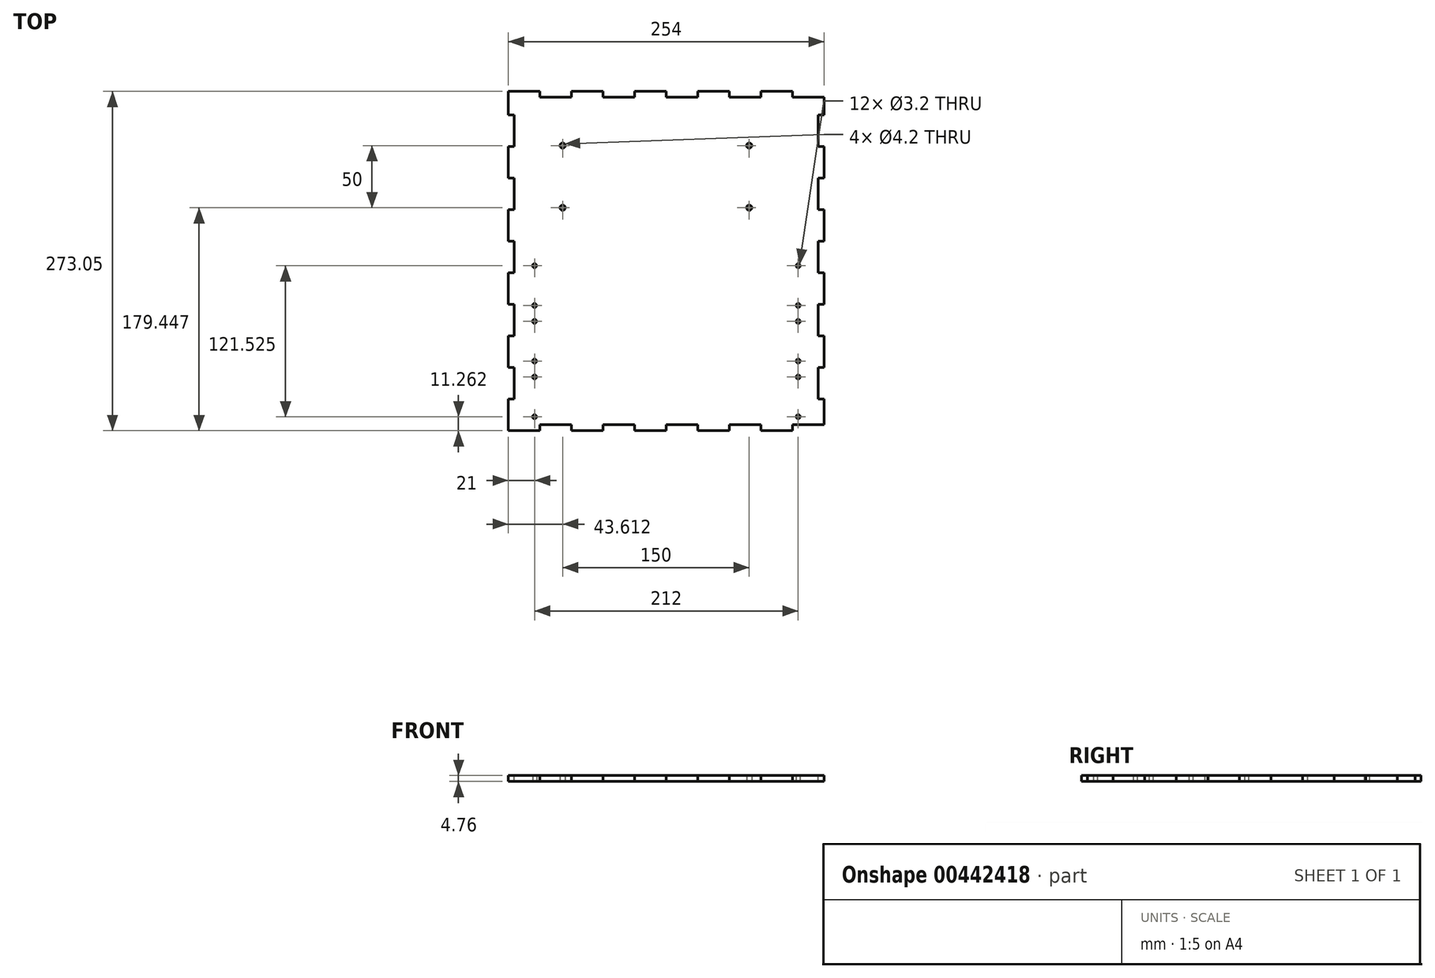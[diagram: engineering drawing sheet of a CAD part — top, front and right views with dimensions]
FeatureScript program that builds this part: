
annotation { "Feature Type Name" : "Feature", "Feature Type Description" : "" }
export const myFeature = defineFeature(function(context is Context, id is Id, definition is map)
    precondition{}
    {
        {
            var Q0;
            Q0=qCreatedBy(makeId("Top.planeOp"),FACE);
            var sketch = newSketch(context, id + "F0", { "sketchPlane" : qUnion([Q0])});
            skLineSegment(sketch, "E0.bottom", {"start": v(0, 0) * mm, "end": v(254, 0) * mm});
            skLineSegment(sketch, "E0.top", {"start": v(0, 273.05) * mm, "end": v(254, 273.05) * mm});
            skLineSegment(sketch, "E0.left", {"start": v(0, 0) * mm, "end": v(0, 273.05) * mm});
            skLineSegment(sketch, "E0.right", {"start": v(254, 0) * mm, "end": v(254, 273.05) * mm});
            skLineSegment(sketch, "E1.0", {"start": v(4.76, 4.76) * mm, "end": v(4.76, 268.29) * mm, "construction": true});
            skLineSegment(sketch, "E1.1", {"start": v(4.76, 4.76) * mm, "end": v(249.24, 4.76) * mm, "construction": true});
            skLineSegment(sketch, "E1.2", {"start": v(249.24, 4.76) * mm, "end": v(249.24, 268.29) * mm, "construction": true});
            skLineSegment(sketch, "E1.3", {"start": v(4.76, 268.29) * mm, "end": v(249.24, 268.29) * mm, "construction": true});
            skCircle(sketch, "E2", {"center": v(21, 11.26) * mm, "radius": 1.6 * mm});
            skCircle(sketch, "E3.0.1.0", {"center": v(21, 43.26) * mm, "radius": 1.6 * mm});
            skLineSegment(sketch, "E3.direction1", {"start": v(21, 11.26) * mm, "end": v(46.4, 11.26) * mm, "construction": true});
            skLineSegment(sketch, "E3.direction2", {"start": v(21, 11.26) * mm, "end": v(21, 43.26) * mm, "construction": true});
            skCircle(sketch, "E4.MirrorC", {"center": v(233, 43.26) * mm, "radius": 1.6 * mm});
            skCircle(sketch, "E5.MirrorC", {"center": v(233, 11.26) * mm, "radius": 1.6 * mm});
            skLineSegment(sketch, "E6.direction1", {"start": v(21, 43.26) * mm, "end": v(46.4, 43.26) * mm, "construction": true});
            skLineSegment(sketch, "E7.bottom", {"start": v(17, 47.26) * mm, "end": v(237, 47.26) * mm, "construction": true});
            skLineSegment(sketch, "E7.top", {"start": v(17, 7.26) * mm, "end": v(237, 7.26) * mm, "construction": true});
            skLineSegment(sketch, "E7.left", {"start": v(17, 47.26) * mm, "end": v(17, 7.26) * mm, "construction": true});
            skLineSegment(sketch, "E7.right", {"start": v(237, 47.26) * mm, "end": v(237, 7.26) * mm, "construction": true});
            skLineSegment(sketch, "E8.0.1.0", {"start": v(17, 92.02) * mm, "end": v(237, 92.02) * mm, "construction": true});
            skLineSegment(sketch, "E8.0.1.1", {"start": v(17, 52.02) * mm, "end": v(237, 52.02) * mm, "construction": true});
            skLineSegment(sketch, "E8.0.1.2", {"start": v(17, 92.02) * mm, "end": v(17, 52.02) * mm, "construction": true});
            skCircle(sketch, "E8.0.1.3", {"center": v(21, 88.02) * mm, "radius": 1.6 * mm});
            skCircle(sketch, "E8.0.1.4", {"center": v(21, 56.02) * mm, "radius": 1.6 * mm});
            skCircle(sketch, "E8.0.1.5", {"center": v(233, 88.02) * mm, "radius": 1.6 * mm});
            skCircle(sketch, "E8.0.1.6", {"center": v(233, 56.02) * mm, "radius": 1.6 * mm});
            skLineSegment(sketch, "E8.0.1.7", {"start": v(237, 92.02) * mm, "end": v(237, 52.02) * mm, "construction": true});
            skLineSegment(sketch, "E8.0.2.0", {"start": v(17, 136.79) * mm, "end": v(237, 136.79) * mm, "construction": true});
            skLineSegment(sketch, "E8.0.2.1", {"start": v(17, 96.79) * mm, "end": v(237, 96.79) * mm, "construction": true});
            skLineSegment(sketch, "E8.0.2.2", {"start": v(17, 136.79) * mm, "end": v(17, 96.79) * mm, "construction": true});
            skCircle(sketch, "E8.0.2.3", {"center": v(21, 132.79) * mm, "radius": 1.6 * mm});
            skCircle(sketch, "E8.0.2.4", {"center": v(21, 100.79) * mm, "radius": 1.6 * mm});
            skCircle(sketch, "E8.0.2.5", {"center": v(233, 132.79) * mm, "radius": 1.6 * mm});
            skCircle(sketch, "E8.0.2.6", {"center": v(233, 100.79) * mm, "radius": 1.6 * mm});
            skLineSegment(sketch, "E8.0.2.7", {"start": v(237, 136.79) * mm, "end": v(237, 96.79) * mm, "construction": true});
            skLineSegment(sketch, "E8.direction1", {"start": v(17, 47.26) * mm, "end": v(42.4, 47.26) * mm, "construction": true});
            skLineSegment(sketch, "E8.direction2", {"start": v(17, 47.26) * mm, "end": v(17, 92.02) * mm, "construction": true});
            skLineSegment(sketch, "E9.bottom", {"start": v(11.11, 261.95) * mm, "end": v(226.11, 261.95) * mm, "construction": true});
            skLineSegment(sketch, "E9.top", {"start": v(11.11, 146.95) * mm, "end": v(226.11, 146.95) * mm, "construction": true});
            skLineSegment(sketch, "E9.left", {"start": v(11.11, 261.95) * mm, "end": v(11.11, 146.95) * mm, "construction": true});
            skLineSegment(sketch, "E9.right", {"start": v(226.11, 261.95) * mm, "end": v(226.11, 146.95) * mm, "construction": true});
            skLineSegment(sketch, "E10", {"start": v(11.11, 204.45) * mm, "end": v(226.11, 204.45) * mm, "construction": true});
            skCircle(sketch, "E11", {"center": v(193.61, 229.45) * mm, "radius": 2.1 * mm});
            skCircle(sketch, "E12.0.1.0", {"center": v(193.61, 179.45) * mm, "radius": 2.1 * mm});
            skCircle(sketch, "E12.1.0.0", {"center": v(43.61, 229.45) * mm, "radius": 2.1 * mm});
            skCircle(sketch, "E12.1.1.0", {"center": v(43.61, 179.45) * mm, "radius": 2.1 * mm});
            skLineSegment(sketch, "E12.direction1", {"start": v(193.61, 229.45) * mm, "end": v(43.61, 229.45) * mm, "construction": true});
            skLineSegment(sketch, "E12.direction2", {"start": v(193.61, 229.45) * mm, "end": v(193.61, 179.45) * mm, "construction": true});
            skLineSegment(sketch, "E13", {"start": v(127, 0) * mm, "end": v(127, 273.05) * mm, "construction": true});
            skSolve(sketch);
        }
        {
            var Q0;
            Q0 = qSketchRegion(id + "F0", true);
            extrude(context, id + "F1", {"entities" : qUnion([Q0]), "depth" : 4.76 * mm});
        }
        {
            var Q0;
            Q0=makeQuery(id+"F1.opExtrude","CAP_FACE",FACE,{"disambiguationData":[OSD([sQuery(id+"F0.wireOp",EDGE,"E0.bottom"),sQuery(id+"F0.wireOp",EDGE,"E0.top"),sQuery(id+"F0.wireOp",EDGE,"E0.left"),sQuery(id+"F0.wireOp",EDGE,"E0.right"),sQuery(id+"F0.wireOp",EDGE,"E2"),sQuery(id+"F0.wireOp",EDGE,"E3.0.1.0"),sQuery(id+"F0.wireOp",EDGE,"E4.MirrorC"),sQuery(id+"F0.wireOp",EDGE,"E5.MirrorC"),sQuery(id+"F0.wireOp",EDGE,"E8.0.1.3"),sQuery(id+"F0.wireOp",EDGE,"E8.0.1.4"),sQuery(id+"F0.wireOp",EDGE,"E8.0.1.5"),sQuery(id+"F0.wireOp",EDGE,"E8.0.1.6"),sQuery(id+"F0.wireOp",EDGE,"E8.0.2.3"),sQuery(id+"F0.wireOp",EDGE,"E8.0.2.4"),sQuery(id+"F0.wireOp",EDGE,"E8.0.2.5"),sQuery(id+"F0.wireOp",EDGE,"E8.0.2.6"),sQuery(id+"F0.wireOp",EDGE,"E11"),sQuery(id+"F0.wireOp",EDGE,"E12.0.1.0"),sQuery(id+"F0.wireOp",EDGE,"E12.1.0.0"),sQuery(id+"F0.wireOp",EDGE,"E12.1.1.0")])],"isStart":false});
            var sketch = newSketch(context, id + "F2", { "sketchPlane" : qUnion([Q0])});
            skLineSegment(sketch, "E14.0", {"start": v(4.76, 4.76) * mm, "end": v(4.76, 268.29) * mm, "construction": true});
            skLineSegment(sketch, "E14.1", {"start": v(4.76, 4.76) * mm, "end": v(249.24, 4.76) * mm, "construction": true});
            skLineSegment(sketch, "E14.2", {"start": v(249.24, 4.76) * mm, "end": v(249.24, 268.29) * mm, "construction": true});
            skLineSegment(sketch, "E14.3", {"start": v(4.76, 268.29) * mm, "end": v(249.24, 268.29) * mm, "construction": true});
            skLineSegment(sketch, "E15", {"start": v(25.4, 0) * mm, "end": v(25.4, 4.76) * mm});
            skLineSegment(sketch, "E16.1.0.0", {"start": v(50.8, 0) * mm, "end": v(50.8, 4.76) * mm});
            skLineSegment(sketch, "E16.2.0.0", {"start": v(76.2, 0) * mm, "end": v(76.2, 4.76) * mm});
            skLineSegment(sketch, "E16.3.0.0", {"start": v(101.6, 0) * mm, "end": v(101.6, 4.76) * mm});
            skLineSegment(sketch, "E16.4.0.0", {"start": v(127, 0) * mm, "end": v(127, 4.76) * mm});
            skLineSegment(sketch, "E16.5.0.0", {"start": v(152.4, 0) * mm, "end": v(152.4, 4.76) * mm});
            skLineSegment(sketch, "E16.6.0.0", {"start": v(177.8, 0) * mm, "end": v(177.8, 4.76) * mm});
            skLineSegment(sketch, "E16.7.0.0", {"start": v(203.2, 0) * mm, "end": v(203.2, 4.76) * mm});
            skLineSegment(sketch, "E16.8.0.0", {"start": v(228.6, 0) * mm, "end": v(228.6, 4.76) * mm});
            skLineSegment(sketch, "E16.direction1", {"start": v(25.4, 0) * mm, "end": v(50.8, 0) * mm, "construction": true});
            skLineSegment(sketch, "E17", {"start": v(25.4, 4.76) * mm, "end": v(50.8, 4.76) * mm});
            skLineSegment(sketch, "E18", {"start": v(25.4, 0) * mm, "end": v(50.8, 0) * mm});
            skLineSegment(sketch, "E19", {"start": v(76.2, 4.76) * mm, "end": v(101.6, 4.76) * mm});
            skLineSegment(sketch, "E20", {"start": v(76.2, 0) * mm, "end": v(101.6, 0) * mm});
            skLineSegment(sketch, "E21", {"start": v(127, 4.76) * mm, "end": v(152.4, 4.76) * mm});
            skLineSegment(sketch, "E22", {"start": v(127, 0) * mm, "end": v(152.4, 0) * mm});
            skLineSegment(sketch, "E23", {"start": v(177.8, 4.76) * mm, "end": v(203.2, 4.76) * mm});
            skLineSegment(sketch, "E24", {"start": v(203.2, 0) * mm, "end": v(177.8, 0) * mm});
            skLineSegment(sketch, "E25.0.9.0", {"start": v(254, 0) * mm, "end": v(254, 4.76) * mm});
            skLineSegment(sketch, "E26", {"start": v(228.6, 4.76) * mm, "end": v(254, 4.76) * mm});
            skLineSegment(sketch, "E27", {"start": v(254, 0) * mm, "end": v(228.6, 0) * mm});
            skLineSegment(sketch, "E28", {"start": v(0, 136.53) * mm, "end": v(254, 136.53) * mm, "construction": true});
            skLineSegment(sketch, "E29", {"start": v(0, 254) * mm, "end": v(4.76, 254) * mm});
            skLineSegment(sketch, "E30.0.1.0", {"start": v(0, 228.6) * mm, "end": v(4.76, 228.6) * mm});
            skLineSegment(sketch, "E30.0.2.0", {"start": v(0, 203.2) * mm, "end": v(4.76, 203.2) * mm});
            skLineSegment(sketch, "E30.0.3.0", {"start": v(0, 177.8) * mm, "end": v(4.76, 177.8) * mm});
            skLineSegment(sketch, "E30.0.4.0", {"start": v(0, 152.4) * mm, "end": v(4.76, 152.4) * mm});
            skLineSegment(sketch, "E30.0.5.0", {"start": v(0, 127) * mm, "end": v(4.76, 127) * mm});
            skLineSegment(sketch, "E30.0.6.0", {"start": v(0, 101.6) * mm, "end": v(4.76, 101.6) * mm});
            skLineSegment(sketch, "E30.0.7.0", {"start": v(0, 76.2) * mm, "end": v(4.76, 76.2) * mm});
            skLineSegment(sketch, "E30.0.8.0", {"start": v(0, 50.8) * mm, "end": v(4.76, 50.8) * mm});
            skLineSegment(sketch, "E30.0.9.0", {"start": v(0, 25.4) * mm, "end": v(4.76, 25.4) * mm});
            skLineSegment(sketch, "E30.direction1", {"start": v(0, 254) * mm, "end": v(25.4, 254) * mm, "construction": true});
            skLineSegment(sketch, "E30.direction2", {"start": v(0, 254) * mm, "end": v(0, 228.6) * mm, "construction": true});
            skLineSegment(sketch, "E31", {"start": v(0, 254) * mm, "end": v(0, 228.6) * mm});
            skLineSegment(sketch, "E32", {"start": v(4.76, 254) * mm, "end": v(4.76, 228.6) * mm});
            skLineSegment(sketch, "E33", {"start": v(0, 203.2) * mm, "end": v(0, 177.8) * mm});
            skLineSegment(sketch, "E34", {"start": v(4.76, 203.2) * mm, "end": v(4.76, 177.8) * mm});
            skLineSegment(sketch, "E35", {"start": v(0, 152.4) * mm, "end": v(0, 127) * mm});
            skLineSegment(sketch, "E36", {"start": v(4.76, 152.4) * mm, "end": v(4.76, 127) * mm});
            skLineSegment(sketch, "E37", {"start": v(0, 101.6) * mm, "end": v(0, 76.2) * mm});
            skLineSegment(sketch, "E38", {"start": v(4.76, 101.6) * mm, "end": v(4.76, 76.2) * mm});
            skLineSegment(sketch, "E39", {"start": v(0, 50.8) * mm, "end": v(0, 25.4) * mm});
            skLineSegment(sketch, "E40", {"start": v(4.76, 50.8) * mm, "end": v(4.76, 25.4) * mm});
            skLineSegment(sketch, "E41", {"start": v(127, 273.05) * mm, "end": v(127, 0) * mm, "construction": true});
            skLineSegment(sketch, "E42.MirrorCS", {"start": v(254, 228.6) * mm, "end": v(249.24, 228.6) * mm});
            skLineSegment(sketch, "E43.MirrorCS", {"start": v(254, 254) * mm, "end": v(228.6, 254) * mm, "construction": true});
            skLineSegment(sketch, "E44.MirrorCS", {"start": v(254, 203.2) * mm, "end": v(249.24, 203.2) * mm});
            skLineSegment(sketch, "E45.MirrorCS", {"start": v(254, 177.8) * mm, "end": v(249.24, 177.8) * mm});
            skLineSegment(sketch, "E46.MirrorCS", {"start": v(254, 152.4) * mm, "end": v(249.24, 152.4) * mm});
            skLineSegment(sketch, "E47.MirrorCS", {"start": v(254, 127) * mm, "end": v(249.24, 127) * mm});
            skLineSegment(sketch, "E48.MirrorCS", {"start": v(254, 101.6) * mm, "end": v(249.24, 101.6) * mm});
            skLineSegment(sketch, "E49.MirrorCS", {"start": v(254, 76.2) * mm, "end": v(249.24, 76.2) * mm});
            skLineSegment(sketch, "E50.MirrorCS", {"start": v(254, 25.4) * mm, "end": v(249.24, 25.4) * mm});
            skLineSegment(sketch, "E51.MirrorCS", {"start": v(254, 50.8) * mm, "end": v(249.24, 50.8) * mm});
            skLineSegment(sketch, "E52", {"start": v(254, 254) * mm, "end": v(249.24, 254) * mm});
            skLineSegment(sketch, "E53", {"start": v(249.24, 254) * mm, "end": v(249.24, 228.6) * mm});
            skLineSegment(sketch, "E54", {"start": v(254, 228.6) * mm, "end": v(254, 254) * mm});
            skLineSegment(sketch, "E55", {"start": v(249.24, 203.2) * mm, "end": v(249.24, 177.8) * mm});
            skLineSegment(sketch, "E56", {"start": v(254, 203.2) * mm, "end": v(254, 177.8) * mm});
            skLineSegment(sketch, "E57", {"start": v(249.24, 152.4) * mm, "end": v(249.24, 127) * mm});
            skLineSegment(sketch, "E58", {"start": v(254, 127) * mm, "end": v(254, 152.4) * mm});
            skLineSegment(sketch, "E59", {"start": v(249.24, 101.6) * mm, "end": v(249.24, 76.2) * mm});
            skLineSegment(sketch, "E60", {"start": v(254, 76.2) * mm, "end": v(254, 101.6) * mm});
            skLineSegment(sketch, "E61", {"start": v(249.24, 50.8) * mm, "end": v(249.24, 25.4) * mm});
            skLineSegment(sketch, "E62", {"start": v(254, 25.4) * mm, "end": v(254, 50.8) * mm});
            skLineSegment(sketch, "E63.MirrorCS", {"start": v(25.4, 273.05) * mm, "end": v(25.4, 268.29) * mm});
            skLineSegment(sketch, "E64.MirrorCS", {"start": v(50.8, 273.05) * mm, "end": v(50.8, 268.29) * mm});
            skLineSegment(sketch, "E65.MirrorCS", {"start": v(76.2, 273.05) * mm, "end": v(76.2, 268.29) * mm});
            skLineSegment(sketch, "E66.MirrorCS", {"start": v(101.6, 273.05) * mm, "end": v(101.6, 268.29) * mm});
            skLineSegment(sketch, "E67.MirrorCS", {"start": v(127, 273.05) * mm, "end": v(127, 268.29) * mm});
            skLineSegment(sketch, "E68.MirrorCS", {"start": v(152.4, 273.05) * mm, "end": v(152.4, 268.29) * mm});
            skLineSegment(sketch, "E69.MirrorCS", {"start": v(177.8, 273.05) * mm, "end": v(177.8, 268.29) * mm});
            skLineSegment(sketch, "E70.MirrorCS", {"start": v(203.2, 273.05) * mm, "end": v(203.2, 268.29) * mm});
            skLineSegment(sketch, "E71.MirrorCS", {"start": v(228.6, 273.05) * mm, "end": v(228.6, 268.29) * mm});
            skLineSegment(sketch, "E72.MirrorCS", {"start": v(254, 273.05) * mm, "end": v(254, 268.29) * mm});
            skLineSegment(sketch, "E73", {"start": v(25.4, 268.29) * mm, "end": v(50.8, 268.29) * mm});
            skLineSegment(sketch, "E74", {"start": v(25.4, 273.05) * mm, "end": v(50.8, 273.05) * mm});
            skLineSegment(sketch, "E75", {"start": v(76.2, 273.05) * mm, "end": v(101.6, 273.05) * mm});
            skLineSegment(sketch, "E76", {"start": v(76.2, 268.29) * mm, "end": v(101.6, 268.29) * mm});
            skLineSegment(sketch, "E77", {"start": v(127, 273.05) * mm, "end": v(152.4, 273.05) * mm});
            skLineSegment(sketch, "E78", {"start": v(127, 268.29) * mm, "end": v(152.4, 268.29) * mm});
            skLineSegment(sketch, "E79", {"start": v(177.8, 273.05) * mm, "end": v(203.2, 273.05) * mm});
            skLineSegment(sketch, "E80", {"start": v(177.8, 268.29) * mm, "end": v(203.2, 268.29) * mm});
            skLineSegment(sketch, "E81", {"start": v(228.6, 273.05) * mm, "end": v(254, 273.05) * mm});
            skLineSegment(sketch, "E82", {"start": v(228.6, 268.29) * mm, "end": v(254, 268.29) * mm});
            skLineSegment(sketch, "E83.0.0.10", {"start": v(0, 0) * mm, "end": v(4.76, 0) * mm});
            skSolve(sketch);
        }
        {
            var Q0;
            Q0 = qSketchRegion(id + "F2", true);
            extrude(context, id + "F3", {"entities" : qUnion([Q0]), "operationType" : NewBodyOperationType.REMOVE, "oppositeDirection" : true, "depth" : 25.4 * mm});
        }
    });
